# Revit family: Deca_Bacia para caixa acoplada_Piano_P.330
name_source: partatom
category: Plumbing Fixtures
units: mm (PartAtom-declared; Revit-internal decimal feet)

## family parameters
Cut with Voids When Loaded = No
Host = Face
Part Type = Normal
Room Calculation Point = No
Round Connector Dimension = Use Radius
Shared = No

## types (4) — shared parameters
Acompanha o Produto = -
Aprovado por = quattroD
Atendimento ao Cliente = 0800-0117073
Categoria = BACIAS E BIDES
Composição Anel Vedação = Não Possui
Composição Assento = -
Composição Básica = Argila, feldspato, caulim, vidrados e corantes inorgânicos.
Composição Componente = Não Possui
Consumo = 6 lpf
Cor Interna = -
Cor Secundária = -
Cores Componente = -
Criado por = quattroD
Código Pai = P.330
Description = Bacia para caixa acoplada
Diâmetro Ponto de Esgoto = 0.1 m
Diâmetro Água Fria = 0.02 m
Informações Complementares = -
Itens de Instalação = 1201.C.KIT.PCD
Linha = Piano
Manufacturer = Deca
Norma = NBR-16727-1;NBR-16727-2
Peso Líquido (Kg) = 33.807
Pressão máx. funcionamento = -
Pressão mín. Aquec. Acúmulo = -
Pressão mín. Aquec. Passagem = -
Pressão mín. funcionamento = -
Raio Ponto de Esgoto = 0.05 m
Raio Água Fria = 0.01 m
Saída de Esgoto = Saída de Esgoto Vertical
Segmento = Banheiro Luxo
Tipo de dispositivo economizador = -
Tipo de mecanismo utilizado = -
Tipo de rosca de entrada = -
Tipo de rosca de saída = -
URL = www.deca.com.br
Vazão na Pressão máx. (L/min) = -
Vazão na Pressão mín. (L/min) = -
zero-valued in all types: CWFU, Default Elevation, WFU

## per-type parameters (varying)
| type | Combinação | Cor Principal | Material | Model |
| P.330.17_Branco | Deca_Caixa acoplada com acionamento Duo_CD.21F : CD.21F.17_Branco | Branco | Deca_Branco | P.330.17 |
| P.330.22_Marrom Fosco | Deca_Caixa acoplada com acionamento Duo_CD.21F : CD.21F.22_Marrom fosco | Marrom Fosco | Deca_Marrom Fosco | P.330.22 |
| P.330.94_Ebano | Deca_Caixa acoplada com acionamento Duo_CD.21F : CD.21F.95_Ebano | Ébano Fosco | Deca_Ébano | P.330.94 |
| P.330.94_Ébano | Deca_Caixa acoplada com acionamento Duo_CD.21F : CD.21F.95_Ébano | Ébano Fosco | Deca_Ébano | P.330.94 |

## geometry (parser evidence)
native form markers: Sweep x6
no freeform markers — native parametric forms only
